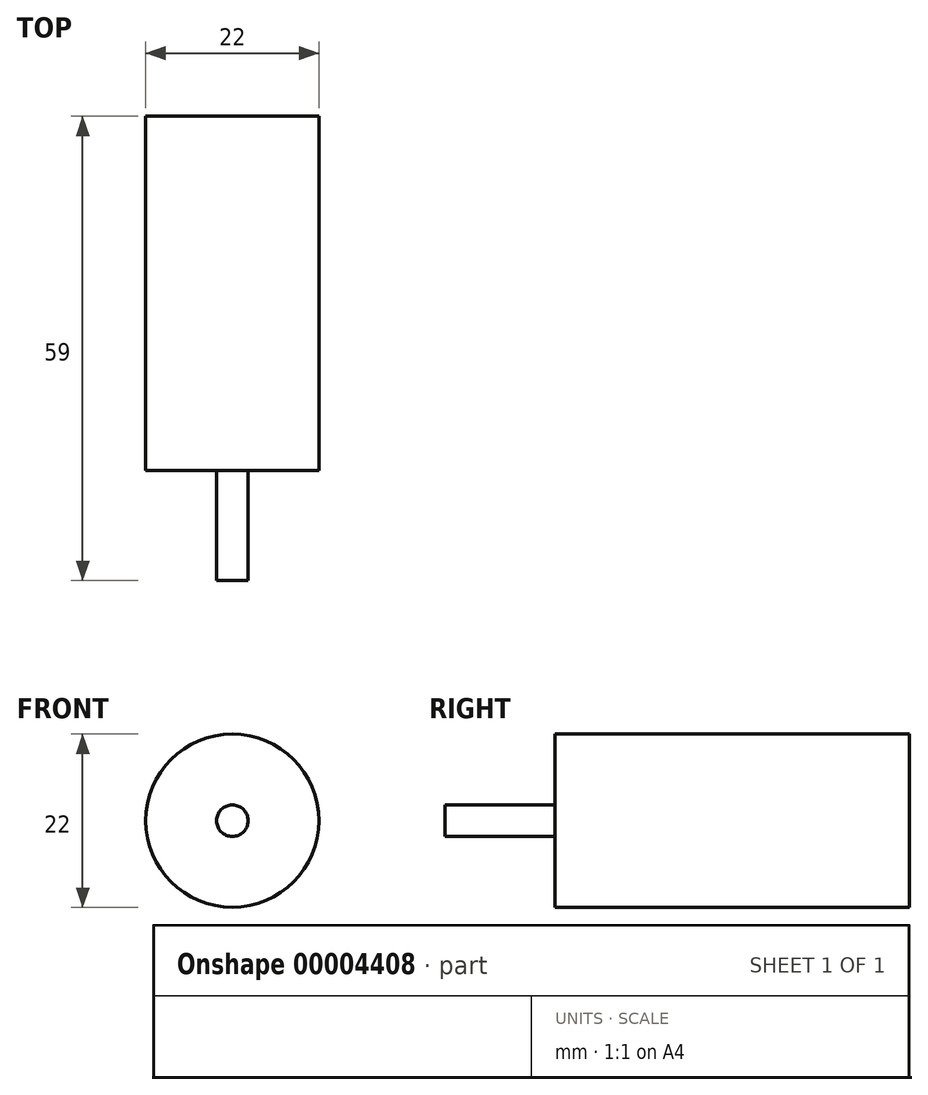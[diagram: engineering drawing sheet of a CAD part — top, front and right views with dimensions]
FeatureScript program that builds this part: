
annotation { "Feature Type Name" : "Feature", "Feature Type Description" : "" }
export const myFeature = defineFeature(function(context is Context, id is Id, definition is map)
    precondition{}
    {
        {
            var Q0;
            Q0=qCreatedBy(makeId("Front.planeOp"),FACE);
            var sketch = newSketch(context, id + "F0", { "sketchPlane" : qUnion([Q0])});
            skCircle(sketch, "E0", {"center": v(0, 0) * mm, "radius": 11 * mm});
            skSolve(sketch);
        }
        {
            var Q0;
            Q0=makeQuery(id+"F0.imprint","IMPRINT",FACE,{"disambiguationData":[TD([[makeQuery(id+"F0.imprint","IMPRINT",EDGE,{"derivedFrom":sQuery(id+"F0.wireOp",EDGE,"E0")}),1.0]])]});
            extrude(context, id + "F1", {"entities" : qUnion([Q0]), "depth" : 29 * mm + 16 * mm});
        }
        {
            var Q0;
            Q0=makeQuery(id+"F1.opExtrude","CAP_FACE",FACE,{"disambiguationData":[OSD([sQuery(id+"F0.wireOp",EDGE,"E0")])],"isStart":false});
            var sketch = newSketch(context, id + "F2", { "sketchPlane" : qUnion([Q0])});
            skCircle(sketch, "E1", {"center": v(0, 0) * mm, "radius": 2 * mm});
            skSolve(sketch);
        }
        {
            var Q0;
            Q0=makeQuery(id+"F2.imprint","IMPRINT",FACE,{"disambiguationData":[TD([[makeQuery(id+"F2.imprint","IMPRINT",EDGE,{"derivedFrom":sQuery(id+"F2.wireOp",EDGE,"E1")}),1.0]])]});
            extrude(context, id + "F3", {"entities" : qUnion([Q0]), "operationType" : NewBodyOperationType.ADD, "depth" : 14 * mm});
        }
    });
